# Revit family: PRD_FrankeWS_Snks_WorkroomSink_SIRW771_SIRW773
name_source: partatom
category: Plumbing Fixtures
revit_build: Autodesk Revit 2018 (Build: 20190510_1515(x64)
units: mm (PartAtom-declared; Revit-internal decimal feet)

## family parameters
Cut with Voids When Loaded = Yes
Host = Face
OmniClass Number = 23.45.05.14.14.17
OmniClass Title = Plaster Sinks
Part Type = Normal
Room Calculation Point = No
Round Connector Dimension = Use Diameter
Shared = Yes

## types (2) — shared parameters
AssetType = Fixed
BowlDepth = 555.00 mm
BowlFinish = High polished
BowlHeight = 283.00 mm
BowlPosition = Center
Brushes = Without brushes
Category = Pr_40_20_96_81, Sinks
Color = Alpine white
Description = Workroom sink made of MIRANIT resin-bonded mineral material with pore-free smooth surface (temperature-resistant up to 80 °C). Basin with integrated tap landing, without tap hole, with marking for drilling holes on the underside of the tap landing. Large inner radii, bottom of basin with 2° slope. Alpine white colour. Drain with under-screwed waste unit including removable sludge bucket, DN 40 overflow at waste unit and DN 25 waste outlet spigot made of stainless steel. Waste unit with DN 40 ball cock completely fitted with tubes. Waste unit rotatable by 90°. Welded substructure frame, powder-coated in basin colour, adjustable base feet. Mounting material included.
DiameterNominal = 40  [stored 0.131234 ft]
DrainSize = 40 mm  [stored 0.131234 ft]
DrainerOrStorage = No
DurationUnit = year
Features = resin-bonded mineral material with pore-free smooth surface
Finish = Coated
Grid = No
IfcExportAs = IfcSanitaryTerminalType
IfcExportType = SINK
IntegralAccessories = incl. mounting material
Manufacturer = KWC Group AG
ManufacturerName = KWC Group AG
ManufacturerURL = www.kwc.com
Material = mineral material
MaterialCode = Miranit
Mounting = Pedestal
NBSDescription = Sinks
NBSReference = 45-35-70/344
NominalDepth = 700 mm  [stored 2.29659 ft]
NominalHeight = 800 mm  [stored 2.62467 ft]
NumberOfWasteHoles = 1
OutletSize = DN 40
Overflow = No
ProductInformation = https://pim.kwc.com
RearUpstand = No
Shape = Cuboid
SinkMaterial = PRD_AR_ResinBondedMaterial_White
SinkType = Plaster
Spillway = No
Splashback = No
StandMaterial = PRD_AR_Black
StrainerMaterial = PRD_AR_StainlessSteel_SatinFinished
Sump = Yes
SumpBasket = Included
TapLedge = Yes
TypeOfMounting = Wall and floor mounting
TypeOfUtilitySink = Cleaner sink
URL = www.kwc.com
Uniclass2015Code = Pr_40_20_96_81
Uniclass2015Title = Sinks
Uniclass2015Version = Products v1.17
UpperEdgeOfBasinHeight = 800.00 mm
Version = 1
WarrantyDurationUnit = year
WashRiffle = No
WasteHolePosition = Center back
WasteHoleProjection = 300.00 mm
zero-valued in all types: Default Elevation, MountingOffset

## per-type parameters (varying)
| type | BIMObjectName | BowlWidth | GrossWeight | ModelNumber | Name | NetWeight | NominalWidth | Size |
| SIRW771 | PRD_AR_Sinks_WorkroomSink_SIRW771 | 1060.00 mm | 103.00 kg | 2000102722 | Workroom Sink SIRW771 | 97.85 kg | 1100 mm | 1100 x 300/800 x 700 mm (W x H x D) |
| SIRW773 | PRD_AR_Sinks_WorkroomSink_SIRW773 | 1960.00 mm | 174.00 kg | 2000102723 | Workroom Sink SIRW773 | 165.30 kg | 2000 mm  [stored 6.56168 ft] | 2000 x 300/800 x 700 mm (W x H x D) |

note: column(s) folded — value = type name in every type: Model, ModelReference

note: [stored X ft] marks values corroborated as IEEE doubles in the binary element streams (Revit-internal decimal feet)

## geometry (parser evidence)
native form markers: Sweep x6
no freeform markers — native parametric forms only
